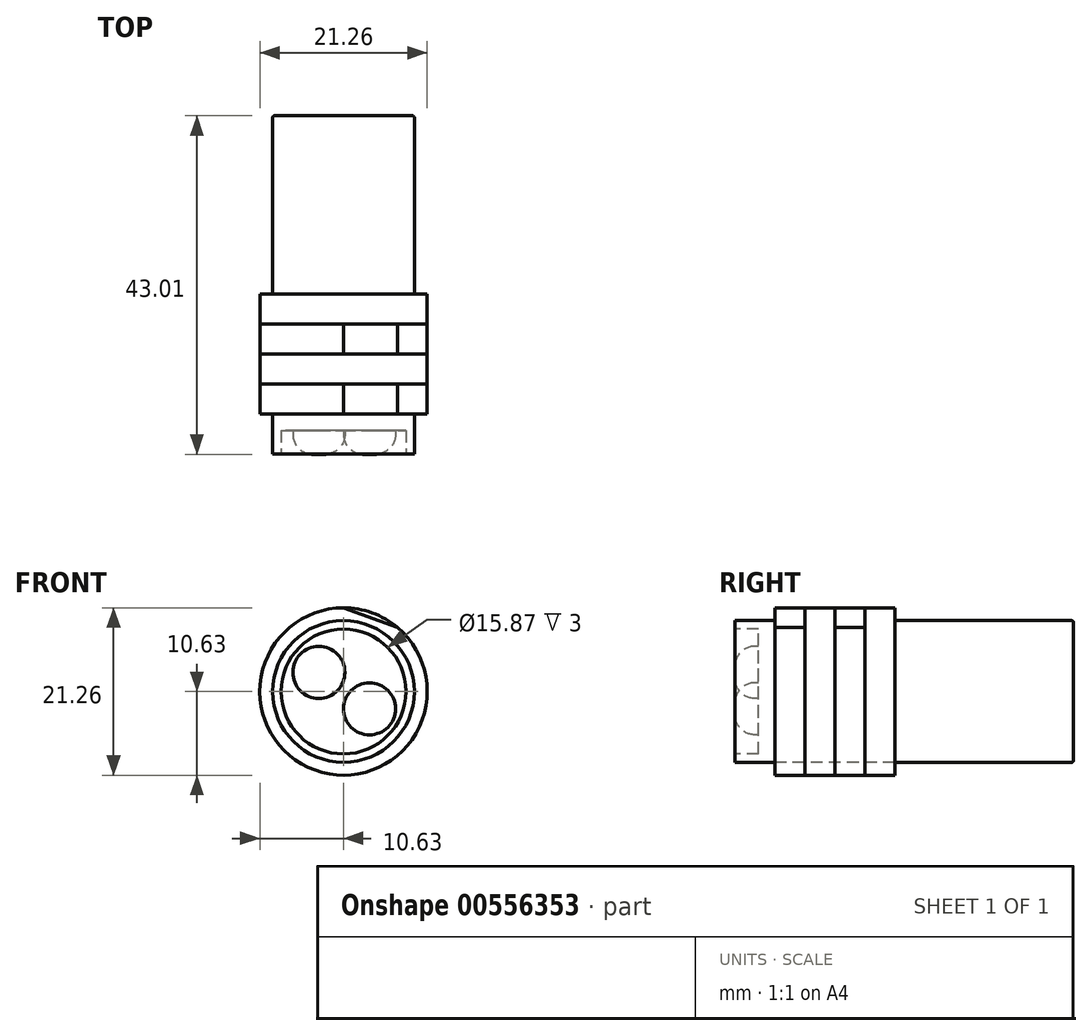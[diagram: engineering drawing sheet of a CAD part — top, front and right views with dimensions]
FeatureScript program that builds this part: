
annotation { "Feature Type Name" : "Feature", "Feature Type Description" : "" }
export const myFeature = defineFeature(function(context is Context, id is Id, definition is map)
    precondition{}
    {
        {
            var Q0;
            Q0=qCreatedBy(makeId("Front.planeOp"),FACE);
            var sketch = newSketch(context, id + "F0", { "sketchPlane" : qUnion([Q0])});
            skCircle(sketch, "E0", {"center": v(0, 0) * mm, "radius": 9 * mm});
            skSolve(sketch);
        }
        {
            var Q0;
            Q0 = qSketchRegion(id + "F0", true);
            extrude(context, id + "F1", {"entities" : qUnion([Q0]), "oppositeDirection" : true, "depth" : 43 * mm, "offsetDistance" : 25.4 * mm});
        }
        {
            var Q0;
            Q0=makeQuery(id+"F1.opExtrude","CAP_FACE",FACE,{"disambiguationData":[OSD([sQuery(id+"F0.wireOp",EDGE,"E0")])],"isStart":true});
            var sketch = newSketch(context, id + "F2", { "sketchPlane" : qUnion([Q0])});
            skCircle(sketch, "E1", {"center": v(0, 0) * mm, "radius": 7.93 * mm});
            skCircle(sketch, "E2", {"center": v(-3.13, 2.43) * mm, "radius": 3.3 * mm});
            skCircle(sketch, "E3", {"center": v(3.3, -2.2) * mm, "radius": 3.3 * mm});
            skSolve(sketch);
        }
        {
            var Q0;
            Q0=makeQuery(id+"F2.imprint","IMPRINT",FACE,{"disambiguationData":[TD([[makeQuery(id+"F2.imprint","IMPRINT",EDGE,{"derivedFrom":sQuery(id+"F2.wireOp",EDGE,"E1")}),1.0]])]});
            extrude(context, id + "F3", {"entities" : qUnion([Q0]), "operationType" : NewBodyOperationType.REMOVE, "oppositeDirection" : true, "depth" : 3 * mm, "offsetDistance" : 25.4 * mm});
        }
        {
            var Q0;
            Q0=makeQuery(id+"F3.boolean.opBoolean","SPLIT",FACE,{"disambiguationData":[TD([makeQuery(id+"F3.opExtrude","SWEPT_FACE",FACE,{"disambiguationData":[OSD([sQuery(id+"F2.wireOp",EDGE,"E2")])]})])],"derivedFrom":makeQuery(id+"F1.opExtrude","CAP_FACE",FACE,{"disambiguationData":[OSD([sQuery(id+"F0.wireOp",EDGE,"E0")])],"isStart":true})});
            var Q1;
            Q1=makeQuery(id+"F3.boolean.opBoolean","SPLIT",FACE,{"disambiguationData":[TD([makeQuery(id+"F3.opExtrude","SWEPT_FACE",FACE,{"disambiguationData":[OSD([sQuery(id+"F2.wireOp",EDGE,"E3")])]})])],"derivedFrom":makeQuery(id+"F1.opExtrude","CAP_FACE",FACE,{"disambiguationData":[OSD([sQuery(id+"F0.wireOp",EDGE,"E0")])],"isStart":true})});
            extrude(context, id + "F4", {"entities" : qUnion([Q0, Q1]), "operationType" : NewBodyOperationType.ADD, "depth" : 0 * mm, "offsetDistance" : 25.4 * mm});
        }
        {
            var Q0;
            Q0=makeQuery(id+"F4.opExtrude","CAP_EDGE",EDGE,{"disambiguationData":[OSD([sQuery(id+"F2.wireOp",EDGE,"E2")])],"isStart":false});
            var Q1;
            Q1=makeQuery(id+"F4.opExtrude","CAP_EDGE",EDGE,{"disambiguationData":[OSD([sQuery(id+"F2.wireOp",EDGE,"E3")])],"isStart":false});
            fillet(context, id + "F5", {"entities" : qUnion([Q0, Q1]), "radius" : 2.54 * mm, "tangentPropagation" : true, "allowEdgeOverflow" : false});
        }
        {
            var Q0;
            Q0=makeQuery(id+"F1.opExtrude","CAP_EDGE",EDGE,{"disambiguationData":[OSD([sQuery(id+"F0.wireOp",EDGE,"E0")])],"isStart":false});
            fillet(context, id + "F6", {"entities" : qUnion([Q0]), "radius" : 0.25 * mm, "tangentPropagation" : true, "allowEdgeOverflow" : false});
        }
        {
            var Q0;
            Q0=qCreatedBy(makeId("Front.planeOp"),FACE);
            cPlane(context, id + "F7", {"entities" : qUnion([Q0]), "cplaneType" : CPlaneType.OFFSET, "offset" : 5.08 * mm, "oppositeDirection" : true, "width" : 152.4 * mm, "height" : 152.4 * mm});
        }
        {
            var Q0;
            Q0=qCreatedBy(id+"F7.planeOp",FACE);
            var sketch = newSketch(context, id + "F8", { "sketchPlane" : qUnion([Q0])});
            skCircle(sketch, "E4", {"center": v(0, 0) * mm, "radius": 10.63 * mm});
            skSolve(sketch);
        }
        {
            var Q0;
            Q0 = qSketchRegion(id + "F8", true);
            extrude(context, id + "F9", {"entities" : qUnion([Q0]), "oppositeDirection" : true, "depth" : 3.8 * mm, "offsetDistance" : 25.4 * mm});
        }
        {
            var Q0;
            Q0=makeQuery(id+"F9.opExtrude","CAP_FACE",FACE,{"disambiguationData":[OSD([sQuery(id+"F8.wireOp",EDGE,"E4")])],"isStart":false});
            extrude(context, id + "F10", {"entities" : qUnion([Q0]), "depth" : 3.8 * mm, "offsetDistance" : 25.4 * mm});
        }
        {
            var Q0;
            Q0=makeQuery(id+"F10.opExtrude","CAP_FACE",FACE,{"disambiguationData":[OSD([sQuery(id+"F8.wireOp",EDGE,"E4")])],"isStart":false});
            extrude(context, id + "F11", {"entities" : qUnion([Q0]), "depth" : 3.8 * mm, "offsetDistance" : 25.4 * mm});
        }
        {
            var Q0;
            Q0=makeQuery(id+"F11.opExtrude","CAP_FACE",FACE,{"disambiguationData":[OSD([sQuery(id+"F8.wireOp",EDGE,"E4")])],"isStart":false});
            extrude(context, id + "F12", {"entities" : qUnion([Q0]), "depth" : 3.8 * mm, "offsetDistance" : 25.4 * mm});
        }
        {
            var Q0;
            Q0=makeQuery(id+"F9.opExtrude","CAP_FACE",FACE,{"disambiguationData":[OSD([sQuery(id+"F8.wireOp",EDGE,"E4")])],"isStart":true});
            var sketch = newSketch(context, id + "F13", { "sketchPlane" : qUnion([Q0])});
            skLineSegment(sketch, "E5", {"start": v(0, 10.63) * mm, "end": v(6.83, 8.14) * mm});
            skCircle(sketch, "E6.0.0", {"center": v(0, 0) * mm, "radius": 10.63 * mm});
            skLineSegment(sketch, "E7", {"start": v(0, 10.63) * mm, "end": v(0, 0) * mm, "construction": true});
            skSolve(sketch);
        }
        {
            var Q0;
            {var subQ0=sQuery(id+"F13.wireOp",EDGE,"E5");Q0=makeQuery(id+"F13.imprint","IMPRINT",FACE,{"disambiguationData":[TD([[makeQuery(id+"F13.imprint","IMPRINT",EDGE,{"derivedFrom":subQ0}),1.0]])]});}
            extrude(context, id + "F14", {"entities" : qUnion([Q0]), "operationType" : NewBodyOperationType.REMOVE, "oppositeDirection" : true, "depth" : 3.8 * mm, "offsetDistance" : 25.4 * mm});
        }
        {
            var Q0;
            Q0=makeQuery(id+"F11.opExtrude","CAP_FACE",FACE,{"disambiguationData":[OSD([sQuery(id+"F8.wireOp",EDGE,"E4")])],"isStart":true});
            var sketch = newSketch(context, id + "F15", { "sketchPlane" : qUnion([Q0])});
            skCircle(sketch, "E8.0", {"center": v(0, 0) * mm, "radius": 10.63 * mm});
            skLineSegment(sketch, "E9", {"start": v(0, 0) * mm, "end": v(0, 10.63) * mm});
            skLineSegment(sketch, "E10", {"start": v(0, 10.63) * mm, "end": v(6.83, 8.14) * mm});
            skSolve(sketch);
        }
        {
            var Q0;
            {var subQ0=sQuery(id+"F15.wireOp",EDGE,"E10");Q0=makeQuery(id+"F15.imprint","IMPRINT",FACE,{"disambiguationData":[TD([[makeQuery(id+"F15.imprint","IMPRINT",EDGE,{"derivedFrom":subQ0}),1.0]])]});}
            extrude(context, id + "F16", {"entities" : qUnion([Q0]), "operationType" : NewBodyOperationType.REMOVE, "oppositeDirection" : true, "depth" : 3.8 * mm, "offsetDistance" : 25.4 * mm});
        }
    });
